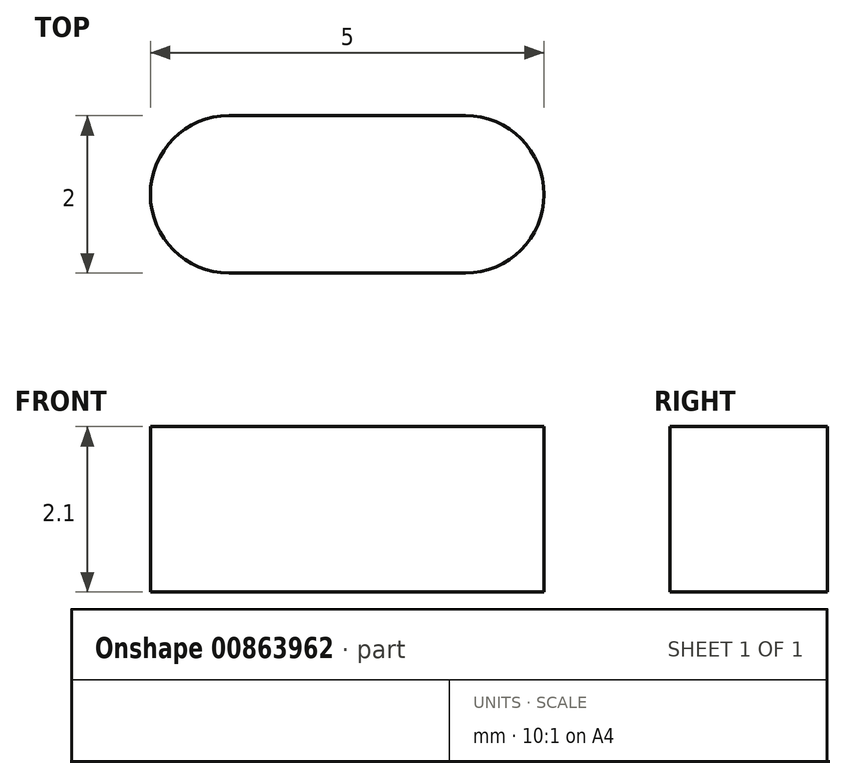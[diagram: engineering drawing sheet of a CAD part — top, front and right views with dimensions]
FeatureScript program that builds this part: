
annotation { "Feature Type Name" : "Feature", "Feature Type Description" : "" }
export const myFeature = defineFeature(function(context is Context, id is Id, definition is map)
    precondition{}
    {
        {
            var Q0;
            Q0=qCreatedBy(makeId("Top.planeOp"),FACE);
            var sketch = newSketch(context, id + "F0", { "sketchPlane" : qUnion([Q0])});
            skLineSegment(sketch, "E0.bottom", {"start": v(2.5, 1) * mm, "end": v(-2.5, 1) * mm});
            skLineSegment(sketch, "E0.top", {"start": v(2.5, -1) * mm, "end": v(-2.5, -1) * mm});
            skLineSegment(sketch, "E0.left", {"start": v(2.5, 1) * mm, "end": v(2.5, -1) * mm});
            skLineSegment(sketch, "E0.right", {"start": v(-2.5, 1) * mm, "end": v(-2.5, -1) * mm});
            skPoint(sketch, "E0.middle", {"position": v(0, 0) * mm});
            skSolve(sketch);
        }
        {
            var Q0;
            Q0 = qSketchRegion(id + "F0", true);
            extrude(context, id + "F1", {"entities" : qUnion([Q0]), "depth" : 2.1 * mm, "offsetDistance" : 25 * mm});
        }
        {
            var Q0;
            Q0=makeQuery(id+"F1.opExtrude","SWEPT_EDGE",EDGE,{"disambiguationData":[OSD([sQuery(id+"F0.wireOp",EDGE,"E0.bottom"),sQuery(id+"F0.wireOp",EDGE,"E0.left")])]});
            var Q1;
            Q1=makeQuery(id+"F1.opExtrude","SWEPT_EDGE",EDGE,{"disambiguationData":[OSD([sQuery(id+"F0.wireOp",EDGE,"E0.top"),sQuery(id+"F0.wireOp",EDGE,"E0.left")])]});
            var Q2;
            Q2=makeQuery(id+"F1.opExtrude","SWEPT_EDGE",EDGE,{"disambiguationData":[OSD([sQuery(id+"F0.wireOp",EDGE,"E0.top"),sQuery(id+"F0.wireOp",EDGE,"E0.right")])]});
            var Q3;
            Q3=makeQuery(id+"F1.opExtrude","SWEPT_EDGE",EDGE,{"disambiguationData":[OSD([sQuery(id+"F0.wireOp",EDGE,"E0.bottom"),sQuery(id+"F0.wireOp",EDGE,"E0.right")])]});
            fillet(context, id + "F2", {"entities" : qUnion([Q0, Q1, Q2, Q3]), "radius" : 1 * mm, "tangentPropagation" : true, "allowEdgeOverflow" : false});
        }
    });
